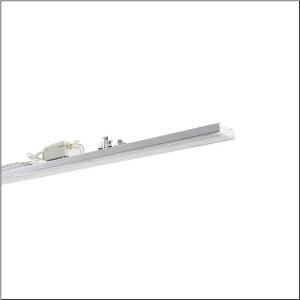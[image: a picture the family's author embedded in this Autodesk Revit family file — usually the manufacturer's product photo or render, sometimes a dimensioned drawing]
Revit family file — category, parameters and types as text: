
# Revit family: licross_r__21_recessed_mo_52te19cn485g_8aa0
name_source: partatom
category: Lighting Fixtures
units: mm (PartAtom-declared; Revit-internal decimal feet)

## family parameters
Cut with Voids When Loaded = No
Host = Face
Light Source = No
Part Type = Normal
Room Calculation Point = No
Round Connector Dimension = Use Diameter
Shared = No

## types (1)
- --- (1 x LED, 8870 lm, 49.9 W, 4000K)
    Apparent Load = 50 VA
    CIE Flux Codes = 55 90 98 100 100
    Color Rendering = 80
    Color Temperature = 4000K
    Default Elevation = 1800 mm
    Description = Licross® 21 Recessed MO, luminaire insert, of sheet steel, galvanised, coil coated, white, length: 1.500mm, width: 66mm, height: 67mm, LED rated luminous flux: 8.880lm, light colour: 840, control gear: ON/OFF Multilumen, CLOi, control gear: ECG DALI, with plug, 5-pole, with phase selection, mains connection: 220..240V, AC, 50/60Hz, start of lifetime: 50W, end of service life: 61W, halogen-free wiring, primary light control with lens, of plastic, primary optical cover: cover, of PMMA, light emission: direct distribution, primary light characteristic: double asymmetric, protection rating (complete): IP54, insulation class (complete): insulation class I (protective earthing), certification: CE, ENEC, VDE, UKCA, protection symbol: D if used in an environment with non-conductive dust loads with corresponding accessories, impact resistance: IK06, permissible ambient temperature for indoor applications: -35..+40°C, corresponds to IFS (International Featured Standards) requirements for safety and quality in the food industry, reducing of maximum allowable ambient temperature of 5°C with ceiling mounting, LABS conformity tested according to VDMA 24364:2018-05, packaging unit: 1 piece
    Height = 58 mm
    Lamp = 1 x LED
    Lamp Light Flux = 8870 lm
    Lamp Power = 49.9 W
    Lamp count = 1
    Length = 1500 mm
    Luminous efficacy = 178 lm/W
    Manufacturer = Siteco
    ModVariant = No
    Model = 52TE19CN485G
    Mounting Place = Ceiling
    Mounting Type = Pendant
    Number of Poles = 1
    OnlyDefault = Yes
    Power Factor = 1
    Product Name = Licross® 21 Recessed MO
    Product group = luminaire insert
    ProductGroupID = 901
    Protection Class = Protection class I
    Protection Degree = IP 54
    RLX_Detail_Level = 1
    RLX_Emergency_Light_Flux = 0 lm
    RLX_Emergency_Type = 0
    RLX_Emergency_Type_DB = No
    RlxData = <blob elided: 22321 chars, md5=0ec38b1b>
    Socket = socket
    Standby Power = 0 W
    System Light Flux = 8870 lm
    System Power = 50 W
    Type Comments = factory setting: luminous flux: 100 % | (A | C | E) | 116 mA
    Type Image = l_1296930.jpg
    URL = http://relux.com
    VarID = @adj_040881
    Voltage = 0 V
    Weight = 0.00 kg
    Width = 66 mm

## geometry (parser evidence)
native form markers: Blend x4, Sweep x11
no freeform markers — native parametric forms only
